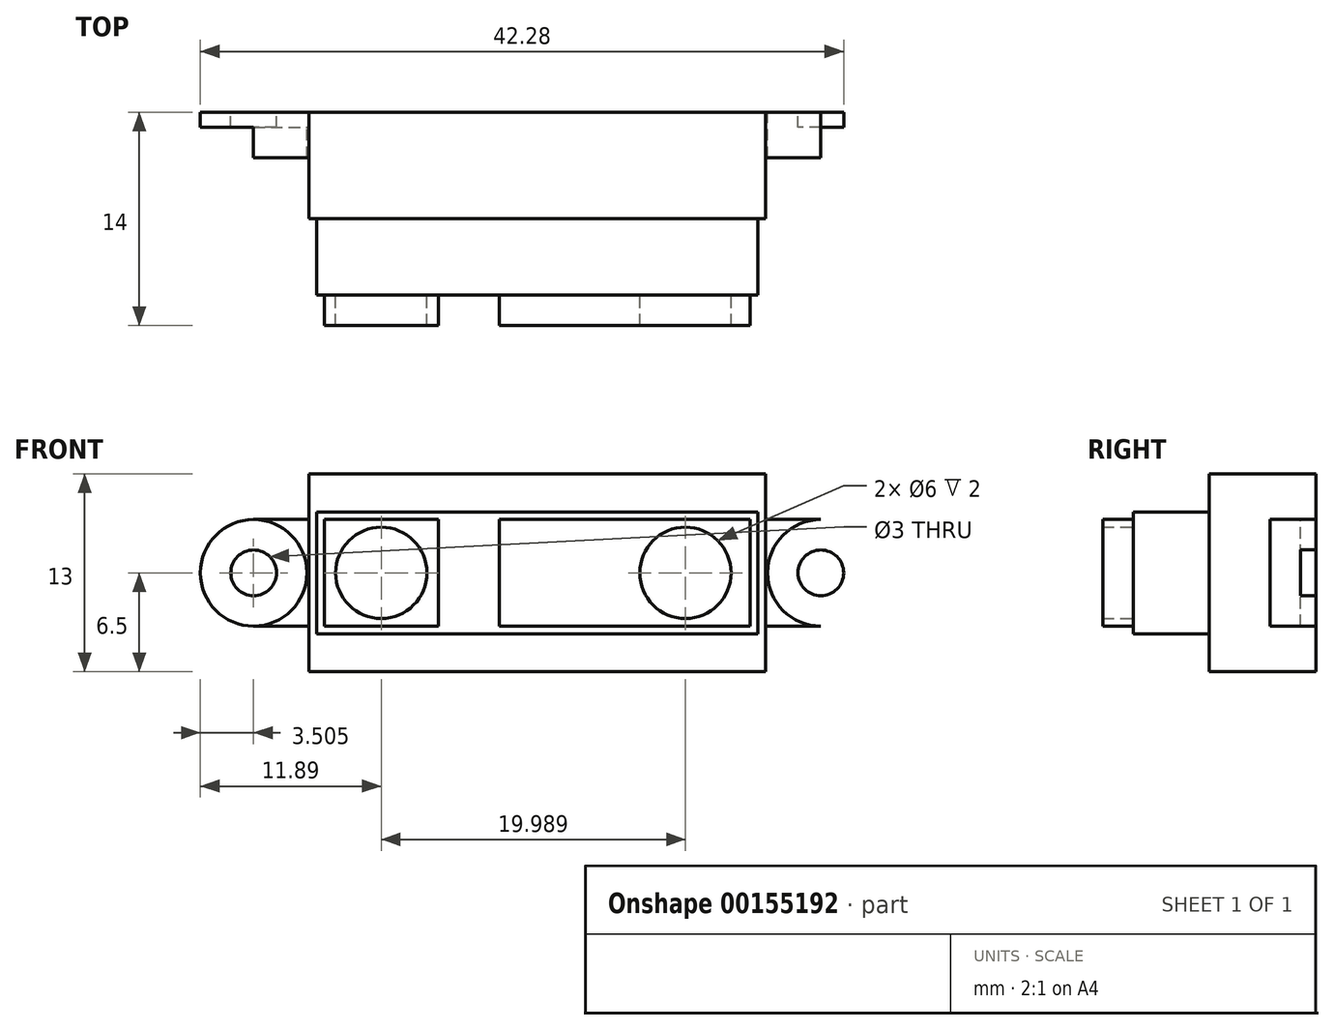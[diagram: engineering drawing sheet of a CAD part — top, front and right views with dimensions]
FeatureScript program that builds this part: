
annotation { "Feature Type Name" : "Feature", "Feature Type Description" : "" }
export const myFeature = defineFeature(function(context is Context, id is Id, definition is map)
    precondition{}
    {
        {
            var Q0;
            Q0=qCreatedBy(makeId("Front.planeOp"),FACE);
            var sketch = newSketch(context, id + "F0", { "sketchPlane" : qUnion([Q0])});
            skLineSegment(sketch, "E0.bottom", {"start": v(15, 6.5) * mm, "end": v(-15, 6.5) * mm});
            skLineSegment(sketch, "E0.top", {"start": v(15, -6.5) * mm, "end": v(-15, -6.5) * mm});
            skLineSegment(sketch, "E0.left", {"start": v(15, 6.5) * mm, "end": v(15, -6.5) * mm});
            skLineSegment(sketch, "E0.right", {"start": v(-15, 6.5) * mm, "end": v(-15, -6.5) * mm});
            skPoint(sketch, "E0.middle", {"position": v(0, 0) * mm});
            skLineSegment(sketch, "E1.bottom", {"start": v(-15, -3.5) * mm, "end": v(-18.64, -3.5) * mm});
            skLineSegment(sketch, "E1.top", {"start": v(-15, 3.5) * mm, "end": v(-18.64, 3.5) * mm});
            skLineSegment(sketch, "E1.left", {"start": v(-15, -3.5) * mm, "end": v(-15, 3.5) * mm});
            skArc(sketch, "E2", {"start": v(-18.64, 3.5) * mm, "mid": v(-22.14, 0) * mm, "end": v(-18.64, -3.5) * mm});
            skCircle(sketch, "E3", {"center": v(-18.64, 0) * mm, "radius": 1.5 * mm});
            skLineSegment(sketch, "E4.MirrorCS", {"start": v(15, 3.5) * mm, "end": v(18.64, 3.5) * mm});
            skCircle(sketch, "E5.MirrorC", {"center": v(18.64, 0) * mm, "radius": 1.5 * mm});
            skArc(sketch, "E6.MirrorCS", {"start": v(18.64, 3.5) * mm, "mid": v(22.14, 0) * mm, "end": v(18.64, -3.5) * mm});
            skLineSegment(sketch, "E7.MirrorCS", {"start": v(15, -3.5) * mm, "end": v(18.64, -3.5) * mm});
            skCircle(sketch, "E8", {"center": v(18.64, 0) * mm, "radius": 3.5 * mm});
            skCircle(sketch, "E9", {"center": v(-18.64, 0) * mm, "radius": 3.5 * mm});
            skSolve(sketch);
        }
        {
            var Q0;
            {var subQ3=sQuery(id+"F0.wireOp",EDGE,"E0.bottom");Q0=makeQuery(id+"F0.imprint","IMPRINT",FACE,{"disambiguationData":[TD([[makeQuery(id+"F0.imprint","IMPRINT",EDGE,{"derivedFrom":subQ3}),1.0]])]});}
            extrude(context, id + "F1", {"entities" : qUnion([Q0]), "depth" : 7 * mm});
        }
        {
            var Q0;
            Q0=makeQuery(id+"F1.opExtrude","CAP_FACE",FACE,{"disambiguationData":[OSD([sQuery(id+"F0.wireOp",EDGE,"E0.bottom"),sQuery(id+"F0.wireOp",EDGE,"E0.top"),sQuery(id+"F0.wireOp",EDGE,"E0.left"),sQuery(id+"F0.wireOp",EDGE,"E0.right")])],"isStart":false});
            var sketch = newSketch(context, id + "F2", { "sketchPlane" : qUnion([Q0])});
            skLineSegment(sketch, "E10.bottom", {"start": v(14.5, 4) * mm, "end": v(-14.5, 4) * mm});
            skLineSegment(sketch, "E10.top", {"start": v(14.5, -4) * mm, "end": v(-14.5, -4) * mm});
            skLineSegment(sketch, "E10.left", {"start": v(14.5, 4) * mm, "end": v(14.5, -4) * mm});
            skLineSegment(sketch, "E10.right", {"start": v(-14.5, 4) * mm, "end": v(-14.5, -4) * mm});
            skPoint(sketch, "E10.middle", {"position": v(0, 0) * mm});
            skSolve(sketch);
        }
        {
            var Q0;
            Q0=qSketchRegion(id+"F2",true);
            extrude(context, id + "F3", {"entities" : qUnion([Q0]), "operationType" : NewBodyOperationType.ADD, "depth" : 5 * mm});
        }
        {
            var Q0;
            Q0=makeQuery(id+"F3.opExtrude","CAP_FACE",FACE,{"disambiguationData":[OSD([sQuery(id+"F2.wireOp",EDGE,"E10.bottom"),sQuery(id+"F2.wireOp",EDGE,"E10.top"),sQuery(id+"F2.wireOp",EDGE,"E10.left"),sQuery(id+"F2.wireOp",EDGE,"E10.right")])],"isStart":false});
            var sketch = newSketch(context, id + "F4", { "sketchPlane" : qUnion([Q0])});
            skLineSegment(sketch, "E11.bottom", {"start": v(-14, 3.5) * mm, "end": v(-6.5, 3.5) * mm});
            skLineSegment(sketch, "E11.top", {"start": v(-14, -3.5) * mm, "end": v(-6.5, -3.5) * mm});
            skLineSegment(sketch, "E11.left", {"start": v(-14, 3.5) * mm, "end": v(-14, -3.5) * mm});
            skLineSegment(sketch, "E11.right", {"start": v(-6.5, 3.5) * mm, "end": v(-6.5, -3.5) * mm});
            skLineSegment(sketch, "E12", {"start": v(-14, 0) * mm, "end": v(-6.5, 0) * mm});
            skCircle(sketch, "E13", {"center": v(-10.25, 0) * mm, "radius": 3 * mm});
            skLineSegment(sketch, "E14.bottom", {"start": v(-2.5, 3.5) * mm, "end": v(14, 3.5) * mm});
            skLineSegment(sketch, "E14.top", {"start": v(-2.5, -3.5) * mm, "end": v(14, -3.5) * mm});
            skLineSegment(sketch, "E14.left", {"start": v(-2.5, 3.5) * mm, "end": v(-2.5, -3.5) * mm});
            skLineSegment(sketch, "E14.right", {"start": v(14, 3.5) * mm, "end": v(14, -3.5) * mm});
            skCircle(sketch, "E15", {"center": v(9.74, 0) * mm, "radius": 3 * mm});
            skSolve(sketch);
        }
        {
            var Q0;
            {var subQ6=sQuery(id+"F4.wireOp",EDGE,"E11.bottom");Q0=makeQuery(id+"F4.imprint","IMPRINT",FACE,{"disambiguationData":[TD([[makeQuery(id+"F4.imprint","IMPRINT",EDGE,{"derivedFrom":subQ6}),-1.0]])]});}
            var Q1;
            {var subQ5=sQuery(id+"F4.wireOp",EDGE,"E11.top");Q1=makeQuery(id+"F4.imprint","IMPRINT",FACE,{"disambiguationData":[TD([[makeQuery(id+"F4.imprint","IMPRINT",EDGE,{"derivedFrom":subQ5}),1.0]])]});}
            var Q2;
            Q2=makeQuery(id+"F4.imprint","IMPRINT",FACE,{"disambiguationData":[TD([[makeQuery(id+"F4.imprint","IMPRINT",EDGE,{"derivedFrom":sQuery(id+"F4.wireOp",EDGE,"E14.bottom")}),-1.0]])]});
            extrude(context, id + "F5", {"entities" : qUnion([Q0, Q1, Q2]), "operationType" : NewBodyOperationType.ADD, "depth" : 2 * mm});
        }
        {
            var Q0;
            Q0=makeQuery(id+"F0.imprint","IMPRINT",FACE,{"disambiguationData":[TD([[makeQuery(id+"F0.imprint","IMPRINT",EDGE,{"derivedFrom":sQuery(id+"F0.wireOp",EDGE,"E1.bottom")}),-1.0]])]});
            var Q1;
            {var subQ0=sQuery(id+"F0.wireOp",EDGE,"E4.MirrorCS");Q1=makeQuery(id+"F0.imprint","IMPRINT",FACE,{"disambiguationData":[TD([[makeQuery(id+"F0.imprint","IMPRINT",EDGE,{"derivedFrom":subQ0}),-1.0]])]});}
            var Q2;
            Q2=makeQuery(id+"F0.imprint","IMPRINT",FACE,{"disambiguationData":[TD([[makeQuery(id+"F0.imprint","IMPRINT",EDGE,{"derivedFrom":sQuery(id+"F0.wireOp",EDGE,"E3")}),-1.0]])]});
            var Q3;
            Q3=makeQuery(id+"F0.imprint","IMPRINT",FACE,{"disambiguationData":[TD([[makeQuery(id+"F0.imprint","IMPRINT",EDGE,{"derivedFrom":sQuery(id+"F0.wireOp",EDGE,"E5.MirrorC")}),1.0]])]});
            extrude(context, id + "F6", {"entities" : qUnion([Q0, Q1, Q2, Q3]), "operationType" : NewBodyOperationType.ADD, "depth" : 1 * mm});
        }
        {
            var Q0;
            {var subQ0=sQuery(id+"F0.wireOp",EDGE,"E1.bottom");Q0=makeQuery(id+"F0.imprint","IMPRINT",FACE,{"disambiguationData":[TD([[makeQuery(id+"F0.imprint","IMPRINT",EDGE,{"derivedFrom":subQ0}),-1.0]])]});}
            var Q1;
            {var subQ0=sQuery(id+"F0.wireOp",EDGE,"E4.MirrorCS");Q1=makeQuery(id+"F0.imprint","IMPRINT",FACE,{"disambiguationData":[TD([[makeQuery(id+"F0.imprint","IMPRINT",EDGE,{"derivedFrom":subQ0}),-1.0]])]});}
            extrude(context, id + "F7", {"entities" : qUnion([Q0, Q1]), "operationType" : NewBodyOperationType.ADD, "depth" : 3 * mm});
        }
    });
